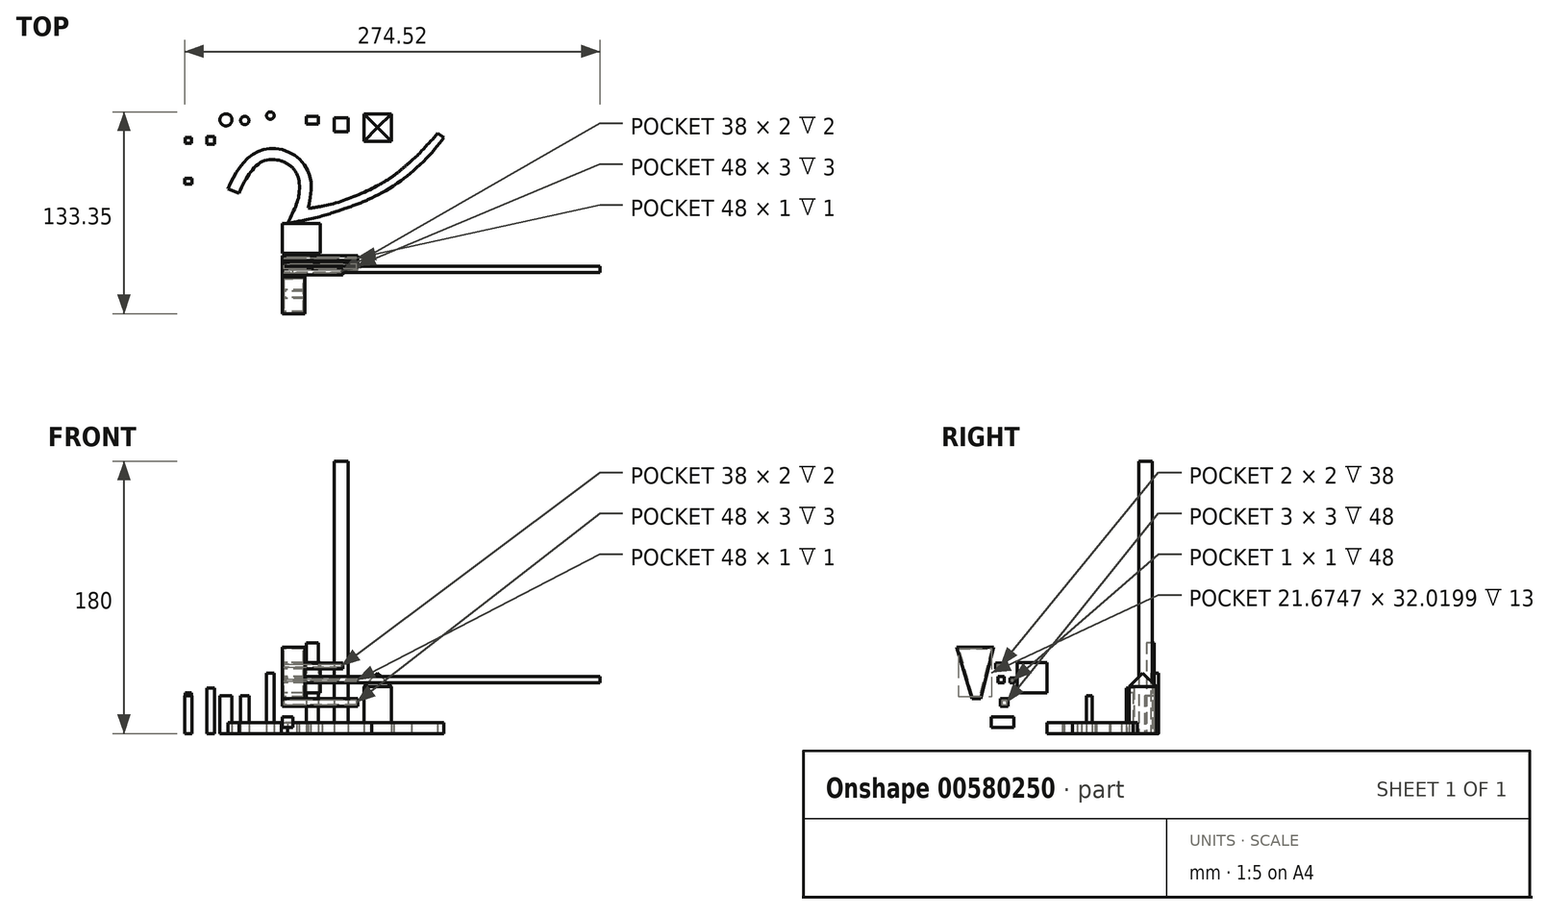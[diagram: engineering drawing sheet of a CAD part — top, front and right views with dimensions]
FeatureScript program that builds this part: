
annotation { "Feature Type Name" : "Feature", "Feature Type Description" : "" }
export const myFeature = defineFeature(function(context is Context, id is Id, definition is map)
    precondition{}
    {
        {
            var Q0;
            Q0=qCreatedBy(makeId("Top.planeOp"),FACE);
            var sketch = newSketch(context, id + "F0", { "sketchPlane" : qUnion([Q0])});
            skFitSpline(sketch, "E0", {"points": [v(-35.91, 9.43) * mm, v(-34, 13.76) * mm, v(-31.5, 18.4) * mm, v(-29.43, 21.7) * mm, v(-26.57, 25.62) * mm, v(-22.93, 29.48) * mm, v(-18.7, 32.55) * mm, v(-14.92, 34.48) * mm, v(-10.85, 35.77) * mm, v(-6.42, 36.13) * mm, v(-0.84, 35.7) * mm, v(5.51, 33.2) * mm, v(9.45, 30.84) * mm, v(13.8, 26.55) * mm, v(17.05, 21.26) * mm, v(18.45, 17.32) * mm, v(19.1, 11.55) * mm, v(18.38, 4.04) * mm, v(17.66, -0.74) * mm, v(17.3, -3.25) * mm], "startDerivative": vector(100.45, 220.55) * mm, "endDerivative": vector(-8.67, -62.76) * mm});
            skFitSpline(sketch, "E1", {"points": [v(17.3, -3.25) * mm, v(19.27, -3.11) * mm, v(21.66, -2.76) * mm, v(24.51, -2.3) * mm, v(26.45, -1.93) * mm], "startDerivative": vector(8.37, 0.4) * mm, "endDerivative": vector(7.88, 1.53) * mm});
            skFitSpline(sketch, "E2", {"points": [v(26.45, -1.93) * mm, v(30.82, -0.98) * mm, v(37, 0.68) * mm, v(43.6, 3.02) * mm, v(50.66, 5.72) * mm, v(58.34, 9.25) * mm, v(63.54, 12) * mm], "startDerivative": vector(30.38, 6.34) * mm, "endDerivative": vector(30.99, 16.93) * mm});
            skFitSpline(sketch, "E3", {"points": [v(63.54, 12) * mm, v(68.49, 14.8) * mm, v(73.84, 18.45) * mm], "startDerivative": vector(10.2, 5.47) * mm, "endDerivative": vector(10.41, 7.4) * mm});
            skFitSpline(sketch, "E4", {"points": [v(73.84, 18.45) * mm, v(77.77, 21.45) * mm, v(81.88, 25) * mm, v(85.57, 28.2) * mm], "startDerivative": vector(12.48, 8.27) * mm, "endDerivative": vector(11.3, 9.41) * mm});
            skFitSpline(sketch, "E5", {"points": [v(85.57, 28.2) * mm, v(91.12, 33.4) * mm, v(94.97, 37.75) * mm, v(98.9, 41.81) * mm, v(102.68, 46.3) * mm], "startDerivative": vector(21.25, 18.99) * mm, "endDerivative": vector(15.23, 18.88) * mm});
            skFitSpline(sketch, "E6", {"points": [v(102.68, 46.3) * mm, v(106.88, 43.5) * mm], "startDerivative": vector(4.2, -2.8) * mm, "endDerivative": vector(4.2, -2.8) * mm});
            skFitSpline(sketch, "E7", {"points": [v(106.88, 43.5) * mm, v(101.45, 36.61) * mm, v(94.83, 29.28) * mm, v(85.57, 20.57) * mm, v(77.93, 14.54) * mm, v(67.24, 7.73) * mm, v(59.13, 3.5) * mm], "startDerivative": vector(-34.95, -45.31) * mm, "endDerivative": vector(-49.54, -24.43) * mm});
            skFitSpline(sketch, "E8", {"points": [v(59.13, 3.5) * mm, v(55.64, 1.88) * mm, v(51.28, 0) * mm, v(46.83, -1.64) * mm, v(41.35, -3.6) * mm, v(37.77, -4.8) * mm], "startDerivative": vector(-18.37, -8.65) * mm, "endDerivative": vector(-18.42, -5.99) * mm});
            skFitSpline(sketch, "E9", {"points": [v(37.77, -4.8) * mm, v(33.78, -6.1) * mm, v(28.43, -7.85) * mm, v(21.27, -9.71) * mm, v(13.39, -11.46) * mm, v(8.88, -12.36) * mm], "startDerivative": vector(-22.87, -7.46) * mm, "endDerivative": vector(-23.54, -4.59) * mm});
            skFitSpline(sketch, "E10", {"points": [v(8.88, -12.36) * mm, v(6.17, -12.88) * mm, v(3.4, -13.46) * mm], "startDerivative": vector(-5.44, -1.02) * mm, "endDerivative": vector(-5.5, -1.17) * mm});
            skFitSpline(sketch, "E11", {"points": [v(3.4, -13.46) * mm, v(5.54, -9.45) * mm, v(7.86, -4.4) * mm, v(9.98, 0.85) * mm, v(11, 5.08) * mm, v(11.34, 11.22) * mm, v(10.73, 16.68) * mm, v(9.57, 19.55) * mm], "startDerivative": vector(15.65, 28.33) * mm, "endDerivative": vector(-11.37, 23.08) * mm});
            skFitSpline(sketch, "E12", {"points": [v(9.57, 19.55) * mm, v(7.74, 22.43) * mm, v(5.06, 25.05) * mm, v(2.14, 26.82) * mm, v(-0.72, 28.03) * mm], "startDerivative": vector(-6.64, 11.76) * mm, "endDerivative": vector(-12.03, 4.77) * mm});
            skFitSpline(sketch, "E13", {"points": [v(-0.72, 28.03) * mm, v(-3.95, 28.7) * mm, v(-8.21, 28.77) * mm, v(-12.05, 28.03) * mm, v(-15.58, 26.09) * mm, v(-19.24, 22.61) * mm, v(-21.92, 19.08) * mm, v(-25.08, 14.03) * mm, v(-27.76, 8.54) * mm, v(-28.56, 6.66) * mm], "startDerivative": vector(-31.55, 8.08) * mm, "endDerivative": vector(-8.54, -21.1) * mm});
            skLineSegment(sketch, "E14", {"start": v(-28.56, 6.66) * mm, "end": v(-35.91, 9.43) * mm});
            skLineSegment(sketch, "E15", {"start": v(-66.1, -50.13) * mm, "end": v(33.9, -50.13) * mm});
            skSolve(sketch);
        }
        {
            var Q0;
            Q0 = qSketchRegion(id + "F0", true);
            extrude(context, id + "F1", {"entities" : qUnion([Q0]), "flatOperationType" : FlatOperationType.REMOVE, "depth" : 7 * mm, "offsetDistance" : 25 * mm, "domain" : OperationDomain.MODEL});
        }
        {
            var Q0;
            Q0=qCreatedBy(makeId("Top.planeOp"),FACE);
            var sketch = newSketch(context, id + "F2", { "sketchPlane" : qUnion([Q0])});
            skCircle(sketch, "E16", {"center": v(-37.16, 55.12) * mm, "radius": 4 * mm});
            skSolve(sketch);
        }
        {
            var Q0;
            Q0=makeQuery(id+"F2.imprint","IMPRINT",FACE,{"disambiguationData":[TD([[makeQuery(id+"F2.imprint","IMPRINT",EDGE,{"derivedFrom":sQuery(id+"F2.wireOp",EDGE,"E16")}),1.0]])]});
            extrude(context, id + "F3", {"entities" : qUnion([Q0]), "depth" : 25 * mm, "offsetDistance" : 25 * mm});
        }
        {
            var Q0;
            Q0=qCreatedBy(makeId("Top.planeOp"),FACE);
            var sketch = newSketch(context, id + "F4", { "sketchPlane" : qUnion([Q0])});
            skCircle(sketch, "E17", {"center": v(-7.84, 57.92) * mm, "radius": 2.5 * mm});
            skSolve(sketch);
        }
        {
            var Q0;
            Q0 = qSketchRegion(id + "F4", true);
            extrude(context, id + "F5", {"entities" : qUnion([Q0]), "depth" : 40 * mm, "offsetDistance" : 25 * mm});
        }
        {
            var Q0;
            Q0=qCreatedBy(makeId("Top.planeOp"),FACE);
            var sketch = newSketch(context, id + "F6", { "sketchPlane" : qUnion([Q0])});
            skLineSegment(sketch, "E18.bottom", {"start": v(16, 57.49) * mm, "end": v(24, 57.49) * mm});
            skLineSegment(sketch, "E18.top", {"start": v(16, 52.49) * mm, "end": v(24, 52.49) * mm});
            skLineSegment(sketch, "E18.left", {"start": v(16, 57.49) * mm, "end": v(16, 52.49) * mm});
            skLineSegment(sketch, "E18.right", {"start": v(24, 57.49) * mm, "end": v(24, 52.49) * mm});
            skSolve(sketch);
        }
        {
            var Q0;
            Q0 = qSketchRegion(id + "F6", true);
            extrude(context, id + "F7", {"entities" : qUnion([Q0]), "depth" : 60 * mm, "offsetDistance" : 25 * mm});
        }
        {
            var Q0;
            Q0=qCreatedBy(makeId("Top.planeOp"),FACE);
            var sketch = newSketch(context, id + "F8", { "sketchPlane" : qUnion([Q0])});
            skLineSegment(sketch, "E19", {"start": v(-53.9, -15) * mm, "end": v(-37.2, -15) * mm});
            skLineSegment(sketch, "E20", {"start": v(-37.2, -15) * mm, "end": v(-37.2, -55) * mm});
            skLineSegment(sketch, "E21", {"start": v(-37.2, -55) * mm, "end": v(-43.2, -55) * mm});
            skLineSegment(sketch, "E22", {"start": v(-43.2, -55) * mm, "end": v(-53.9, -15) * mm});
            skSolve(sketch);
        }
        {
            var Q0;
            Q0=makeQuery(id+"F8.imprint","IMPRINT",FACE,{"disambiguationData":[TD([[makeQuery(id+"F8.imprint","IMPRINT",EDGE,{"derivedFrom":sQuery(id+"F8.wireOp",EDGE,"E19")}),-1.0]])]});
            var Q1;
            Q1=sQuery(id+"F8.wireOp",EDGE,"E20");
            revolve(context, id + "F9", {"entities" : qUnion([Q0]), "axis" : qUnion([Q1]), "revolveType" : RevolveType.FULL});
        }
        {
            var Q0;
            Q0=makeQuery(id+"F9.opRevolve","SWEPT_BODY",BODY,{"disambiguationData":[OSD([sQuery(id+"F8.wireOp",EDGE,"E19"),sQuery(id+"F8.wireOp",EDGE,"E20"),sQuery(id+"F8.wireOp",EDGE,"E21"),sQuery(id+"F8.wireOp",EDGE,"E22")])]});
            deleteBodies(context, id + "F10", {"entities" : qUnion([Q0])});
        }
        {
            var Q0;
            Q0=qCreatedBy(makeId("Top.planeOp"),FACE);
            var sketch = newSketch(context, id + "F11", { "sketchPlane" : qUnion([Q0])});
            skLineSegment(sketch, "E23.bottom", {"start": v(34.48, 56.36) * mm, "end": v(43.48, 56.36) * mm});
            skLineSegment(sketch, "E23.top", {"start": v(34.48, 47.36) * mm, "end": v(43.48, 47.36) * mm});
            skLineSegment(sketch, "E23.left", {"start": v(34.48, 56.36) * mm, "end": v(34.48, 47.36) * mm});
            skLineSegment(sketch, "E23.right", {"start": v(43.48, 56.36) * mm, "end": v(43.48, 47.36) * mm});
            skSolve(sketch);
        }
        {
            var Q0;
            Q0 = qSketchRegion(id + "F11", true);
            extrude(context, id + "F12", {"entities" : qUnion([Q0]), "depth" : 180 * mm, "offsetDistance" : 25 * mm});
        }
        {
            var Q0;
            Q0=qCreatedBy(makeId("Top.planeOp"),FACE);
            var sketch = newSketch(context, id + "F13", { "sketchPlane" : qUnion([Q0])});
            skLineSegment(sketch, "E24.bottom", {"start": v(-64.03, 43.55) * mm, "end": v(-60.03, 43.55) * mm});
            skLineSegment(sketch, "E24.top", {"start": v(-64.03, 39.55) * mm, "end": v(-60.03, 39.55) * mm});
            skLineSegment(sketch, "E24.left", {"start": v(-64.03, 43.55) * mm, "end": v(-64.03, 39.55) * mm});
            skLineSegment(sketch, "E24.right", {"start": v(-60.03, 43.55) * mm, "end": v(-60.03, 39.55) * mm});
            skSolve(sketch);
        }
        {
            var Q0;
            Q0 = qSketchRegion(id + "F13", true);
            extrude(context, id + "F14", {"entities" : qUnion([Q0]), "depth" : 27 * mm, "offsetDistance" : 25 * mm});
        }
        {
            var Q0;
            Q0=qCreatedBy(makeId("Top.planeOp"),FACE);
            var sketch = newSketch(context, id + "F15", { "sketchPlane" : qUnion([Q0])});
            skLineSegment(sketch, "E25.bottom", {"start": v(53.98, 58.98) * mm, "end": v(71.98, 58.98) * mm});
            skLineSegment(sketch, "E25.top", {"start": v(53.98, 40.98) * mm, "end": v(71.98, 40.98) * mm});
            skLineSegment(sketch, "E25.left", {"start": v(53.98, 58.98) * mm, "end": v(53.98, 40.98) * mm});
            skLineSegment(sketch, "E25.right", {"start": v(71.98, 58.98) * mm, "end": v(71.98, 40.98) * mm});
            skSolve(sketch);
        }
        {
            var Q0;
            Q0 = qSketchRegion(id + "F15", true);
            extrude(context, id + "F16", {"entities" : qUnion([Q0]), "depth" : 40 * mm, "offsetDistance" : 25 * mm});
        }
        {
            var Q0;
            Q0=makeQuery(id+"F16.opExtrude","CAP_FACE",FACE,{"disambiguationData":[OSD([sQuery(id+"F15.wireOp",EDGE,"E25.bottom"),sQuery(id+"F15.wireOp",EDGE,"E25.top"),sQuery(id+"F15.wireOp",EDGE,"E25.left"),sQuery(id+"F15.wireOp",EDGE,"E25.right")])],"isStart":false});
            chamfer(context, id + "F17", {"entities" : qUnion([Q0]), "width" : 9 * mm, "tangentPropagation" : true});
        }
        {
            var Q0;
            Q0=qCreatedBy(makeId("Top.planeOp"),FACE);
            var sketch = newSketch(context, id + "F18", { "sketchPlane" : qUnion([Q0])});
            skLineSegment(sketch, "E26.bottom", {"start": v(-64.52, 16.56) * mm, "end": v(-59.52, 16.56) * mm});
            skLineSegment(sketch, "E26.top", {"start": v(-64.52, 12.56) * mm, "end": v(-59.52, 12.56) * mm});
            skLineSegment(sketch, "E26.left", {"start": v(-64.52, 16.56) * mm, "end": v(-64.52, 12.56) * mm});
            skLineSegment(sketch, "E26.right", {"start": v(-59.52, 16.56) * mm, "end": v(-59.52, 12.56) * mm});
            skSolve(sketch);
        }
        {
            var Q0;
            Q0 = qSketchRegion(id + "F18", true);
            extrude(context, id + "F19", {"entities" : qUnion([Q0]), "depth" : 25 * mm, "offsetDistance" : 25 * mm});
        }
        {
            var Q0;
            Q0=qCreatedBy(makeId("Top.planeOp"),FACE);
            var sketch = newSketch(context, id + "F20", { "sketchPlane" : qUnion([Q0])});
            skLineSegment(sketch, "E27.bottom", {"start": v(-49.8, 44.04) * mm, "end": v(-44.8, 44.04) * mm});
            skLineSegment(sketch, "E27.top", {"start": v(-49.8, 39.04) * mm, "end": v(-44.8, 39.04) * mm});
            skLineSegment(sketch, "E27.left", {"start": v(-49.8, 44.04) * mm, "end": v(-49.8, 39.04) * mm});
            skLineSegment(sketch, "E27.right", {"start": v(-44.8, 44.04) * mm, "end": v(-44.8, 39.04) * mm});
            skSolve(sketch);
        }
        {
            var Q0;
            Q0 = qSketchRegion(id + "F20", true);
            extrude(context, id + "F21", {"entities" : qUnion([Q0]), "depth" : 30 * mm, "offsetDistance" : 25 * mm});
        }
        {
            var Q0;
            Q0=qCreatedBy(makeId("Top.planeOp"),FACE);
            var sketch = newSketch(context, id + "F22", { "sketchPlane" : qUnion([Q0])});
            skCircle(sketch, "E28", {"center": v(-24.7, 54.67) * mm, "radius": 2.75 * mm});
            skSolve(sketch);
        }
        {
            var Q0;
            Q0 = qSketchRegion(id + "F22", true);
            extrude(context, id + "F23", {"entities" : qUnion([Q0]), "depth" : 25 * mm, "offsetDistance" : 25 * mm});
        }
        {
            var Q0;
            Q0=qCreatedBy(makeId("Right.planeOp"),FACE);
            var sketch = newSketch(context, id + "F24", { "sketchPlane" : qUnion([Q0])});
            skLineSegment(sketch, "E29.bottom", {"start": v(-41.7, 33.52) * mm, "end": v(-45.7, 33.52) * mm});
            skLineSegment(sketch, "E29.top", {"start": v(-41.7, 37.52) * mm, "end": v(-45.7, 37.52) * mm});
            skLineSegment(sketch, "E29.left", {"start": v(-41.7, 33.52) * mm, "end": v(-41.7, 37.52) * mm});
            skLineSegment(sketch, "E29.right", {"start": v(-45.7, 33.52) * mm, "end": v(-45.7, 37.52) * mm});
            skSolve(sketch);
        }
        {
            var Q0;
            Q0 = qSketchRegion(id + "F24", true);
            extrude(context, id + "F25", {"entities" : qUnion([Q0]), "depth" : 210 * mm, "offsetDistance" : 25 * mm});
        }
        {
            var Q0;
            Q0=qCreatedBy(makeId("Right.planeOp"),FACE);
            var sketch = newSketch(context, id + "F26", { "sketchPlane" : qUnion([Q0])});
            skLineSegment(sketch, "E30.bottom", {"start": v(-37.72, 36.57) * mm, "end": v(-34.72, 36.57) * mm});
            skLineSegment(sketch, "E30.top", {"start": v(-37.72, 33.57) * mm, "end": v(-34.72, 33.57) * mm});
            skLineSegment(sketch, "E30.left", {"start": v(-37.72, 36.57) * mm, "end": v(-37.72, 33.57) * mm});
            skLineSegment(sketch, "E30.right", {"start": v(-34.72, 36.57) * mm, "end": v(-34.72, 33.57) * mm});
            skSolve(sketch);
        }
        {
            var Q0;
            Q0 = qSketchRegion(id + "F26", true);
            extrude(context, id + "F27", {"entities" : qUnion([Q0]), "depth" : 50 * mm, "offsetDistance" : 25 * mm});
        }
        {
            var Q0;
            Q0=qCreatedBy(makeId("Right.planeOp"),FACE);
            var sketch = newSketch(context, id + "F28", { "sketchPlane" : qUnion([Q0])});
            skLineSegment(sketch, "E31.bottom", {"start": v(-32.99, 46.95) * mm, "end": v(-13.25, 46.95) * mm});
            skLineSegment(sketch, "E31.top", {"start": v(-32.99, 26.95) * mm, "end": v(-13.25, 26.95) * mm});
            skLineSegment(sketch, "E31.left", {"start": v(-32.99, 46.95) * mm, "end": v(-32.99, 26.95) * mm});
            skLineSegment(sketch, "E31.right", {"start": v(-13.25, 46.95) * mm, "end": v(-13.25, 26.95) * mm});
            skSolve(sketch);
        }
        {
            var Q0;
            Q0 = qSketchRegion(id + "F28", true);
            extrude(context, id + "F29", {"entities" : qUnion([Q0]), "depth" : 25 * mm, "offsetDistance" : 25 * mm});
        }
        {
            var Q0;
            Q0=qCreatedBy(makeId("Right.planeOp"),FACE);
            var sketch = newSketch(context, id + "F30", { "sketchPlane" : qUnion([Q0])});
            skLineSegment(sketch, "E32.bottom", {"start": v(-47.25, 46.56) * mm, "end": v(-43.25, 46.56) * mm});
            skLineSegment(sketch, "E32.top", {"start": v(-47.25, 42.56) * mm, "end": v(-43.25, 42.56) * mm});
            skLineSegment(sketch, "E32.left", {"start": v(-47.25, 46.56) * mm, "end": v(-47.25, 42.56) * mm});
            skLineSegment(sketch, "E32.right", {"start": v(-43.25, 46.56) * mm, "end": v(-43.25, 42.56) * mm});
            skSolve(sketch);
        }
        {
            var Q0;
            Q0 = qSketchRegion(id + "F30", true);
            extrude(context, id + "F31", {"entities" : qUnion([Q0]), "depth" : 40 * mm, "offsetDistance" : 25 * mm});
        }
        {
            var Q0;
            Q0=qCreatedBy(makeId("Right.planeOp"),FACE);
            var sketch = newSketch(context, id + "F32", { "sketchPlane" : qUnion([Q0])});
            skLineSegment(sketch, "E33", {"start": v(-72.93, 57.16) * mm, "end": v(-48.64, 57.16) * mm});
            skLineSegment(sketch, "E34", {"start": v(-48.64, 57.16) * mm, "end": v(-57.28, 23.14) * mm});
            skLineSegment(sketch, "E35", {"start": v(-57.28, 23.14) * mm, "end": v(-62.97, 23.14) * mm});
            skLineSegment(sketch, "E36", {"start": v(-62.97, 23.14) * mm, "end": v(-72.93, 57.16) * mm});
            skSolve(sketch);
        }
        {
            var Q0;
            Q0 = qSketchRegion(id + "F32", true);
            extrude(context, id + "F33", {"entities" : qUnion([Q0]), "depth" : 15 * mm, "offsetDistance" : 25 * mm});
        }
        {
            var Q0;
            Q0=makeQuery(id+"F33.opExtrude","CAP_FACE",FACE,{"disambiguationData":[OSD([sQuery(id+"F32.wireOp",EDGE,"E33"),sQuery(id+"F32.wireOp",EDGE,"E34"),sQuery(id+"F32.wireOp",EDGE,"E35"),sQuery(id+"F32.wireOp",EDGE,"E36")])],"isStart":false});
            var Q1;
            Q1=makeQuery(id+"F31.opExtrude","CAP_FACE",FACE,{"disambiguationData":[OSD([sQuery(id+"F30.wireOp",EDGE,"E32.bottom"),sQuery(id+"F30.wireOp",EDGE,"E32.top"),sQuery(id+"F30.wireOp",EDGE,"E32.left"),sQuery(id+"F30.wireOp",EDGE,"E32.right")])],"isStart":false});
            var Q2;
            Q2=makeQuery(id+"F27.opExtrude","CAP_FACE",FACE,{"disambiguationData":[OSD([sQuery(id+"F26.wireOp",EDGE,"E30.bottom"),sQuery(id+"F26.wireOp",EDGE,"E30.top"),sQuery(id+"F26.wireOp",EDGE,"E30.left"),sQuery(id+"F26.wireOp",EDGE,"E30.right")])],"isStart":false});
            var Q3;
            Q3=makeQuery(id+"F33.opExtrude","SWEPT_BODY",BODY,{"disambiguationData":[OSD([sQuery(id+"F32.wireOp",EDGE,"E33"),sQuery(id+"F32.wireOp",EDGE,"E34"),sQuery(id+"F32.wireOp",EDGE,"E35"),sQuery(id+"F32.wireOp",EDGE,"E36")])]});
            var Q4;
            Q4=makeQuery(id+"F31.opExtrude","SWEPT_BODY",BODY,{"disambiguationData":[OSD([sQuery(id+"F30.wireOp",EDGE,"E32.bottom"),sQuery(id+"F30.wireOp",EDGE,"E32.top"),sQuery(id+"F30.wireOp",EDGE,"E32.left"),sQuery(id+"F30.wireOp",EDGE,"E32.right")])]});
            var Q5;
            Q5=makeQuery(id+"F27.opExtrude","SWEPT_BODY",BODY,{"disambiguationData":[OSD([sQuery(id+"F26.wireOp",EDGE,"E30.bottom"),sQuery(id+"F26.wireOp",EDGE,"E30.top"),sQuery(id+"F26.wireOp",EDGE,"E30.left"),sQuery(id+"F26.wireOp",EDGE,"E30.right")])]});
            shell(context, id + "F34", {"isHollow" : true, "entities" : qUnion([Q0, Q1, Q2]), "parts" : qUnion([Q3, Q4, Q5]), "thickness" : 1 * mm});
        }
        {
            var Q0;
            Q0=qCreatedBy(makeId("Right.planeOp"),FACE);
            var sketch = newSketch(context, id + "F35", { "sketchPlane" : qUnion([Q0])});
            skLineSegment(sketch, "E37.bottom", {"start": v(-44.12, 23) * mm, "end": v(-39.12, 23) * mm});
            skLineSegment(sketch, "E37.top", {"start": v(-44.12, 18) * mm, "end": v(-39.12, 18) * mm});
            skLineSegment(sketch, "E37.left", {"start": v(-44.12, 23) * mm, "end": v(-44.12, 18) * mm});
            skLineSegment(sketch, "E37.right", {"start": v(-39.12, 23) * mm, "end": v(-39.12, 18) * mm});
            skSolve(sketch);
        }
        {
            var Q0;
            Q0 = qSketchRegion(id + "F35", true);
            extrude(context, id + "F36", {"entities" : qUnion([Q0]), "depth" : 50 * mm, "offsetDistance" : 25 * mm});
        }
        {
            var Q0;
            Q0=makeQuery(id+"F36.opExtrude","CAP_FACE",FACE,{"disambiguationData":[OSD([sQuery(id+"F35.wireOp",EDGE,"E37.bottom"),sQuery(id+"F35.wireOp",EDGE,"E37.top"),sQuery(id+"F35.wireOp",EDGE,"E37.left"),sQuery(id+"F35.wireOp",EDGE,"E37.right")])],"isStart":false});
            var Q1;
            Q1=makeQuery(id+"F36.opExtrude","SWEPT_BODY",BODY,{"disambiguationData":[OSD([sQuery(id+"F35.wireOp",EDGE,"E37.bottom"),sQuery(id+"F35.wireOp",EDGE,"E37.top"),sQuery(id+"F35.wireOp",EDGE,"E37.left"),sQuery(id+"F35.wireOp",EDGE,"E37.right")])]});
            shell(context, id + "F37", {"isHollow" : true, "entities" : qUnion([Q0]), "parts" : qUnion([Q1]), "thickness" : 1 * mm});
        }
        {
            var Q0;
            Q0=qCreatedBy(makeId("Right.planeOp"),FACE);
            var sketch = newSketch(context, id + "F38", { "sketchPlane" : qUnion([Q0])});
            skLineSegment(sketch, "E38.bottom", {"start": v(-50.18, 10.99) * mm, "end": v(-35.18, 10.99) * mm});
            skLineSegment(sketch, "E38.top", {"start": v(-50.18, 3.99) * mm, "end": v(-35.18, 3.99) * mm});
            skLineSegment(sketch, "E38.left", {"start": v(-50.18, 10.99) * mm, "end": v(-50.18, 3.99) * mm});
            skLineSegment(sketch, "E38.right", {"start": v(-35.18, 10.99) * mm, "end": v(-35.18, 3.99) * mm});
            skSolve(sketch);
        }
        {
            var Q0;
            Q0 = qSketchRegion(id + "F38", true);
            extrude(context, id + "F39", {"entities" : qUnion([Q0]), "depth" : 7 * mm, "offsetDistance" : 25 * mm});
        }
    });
